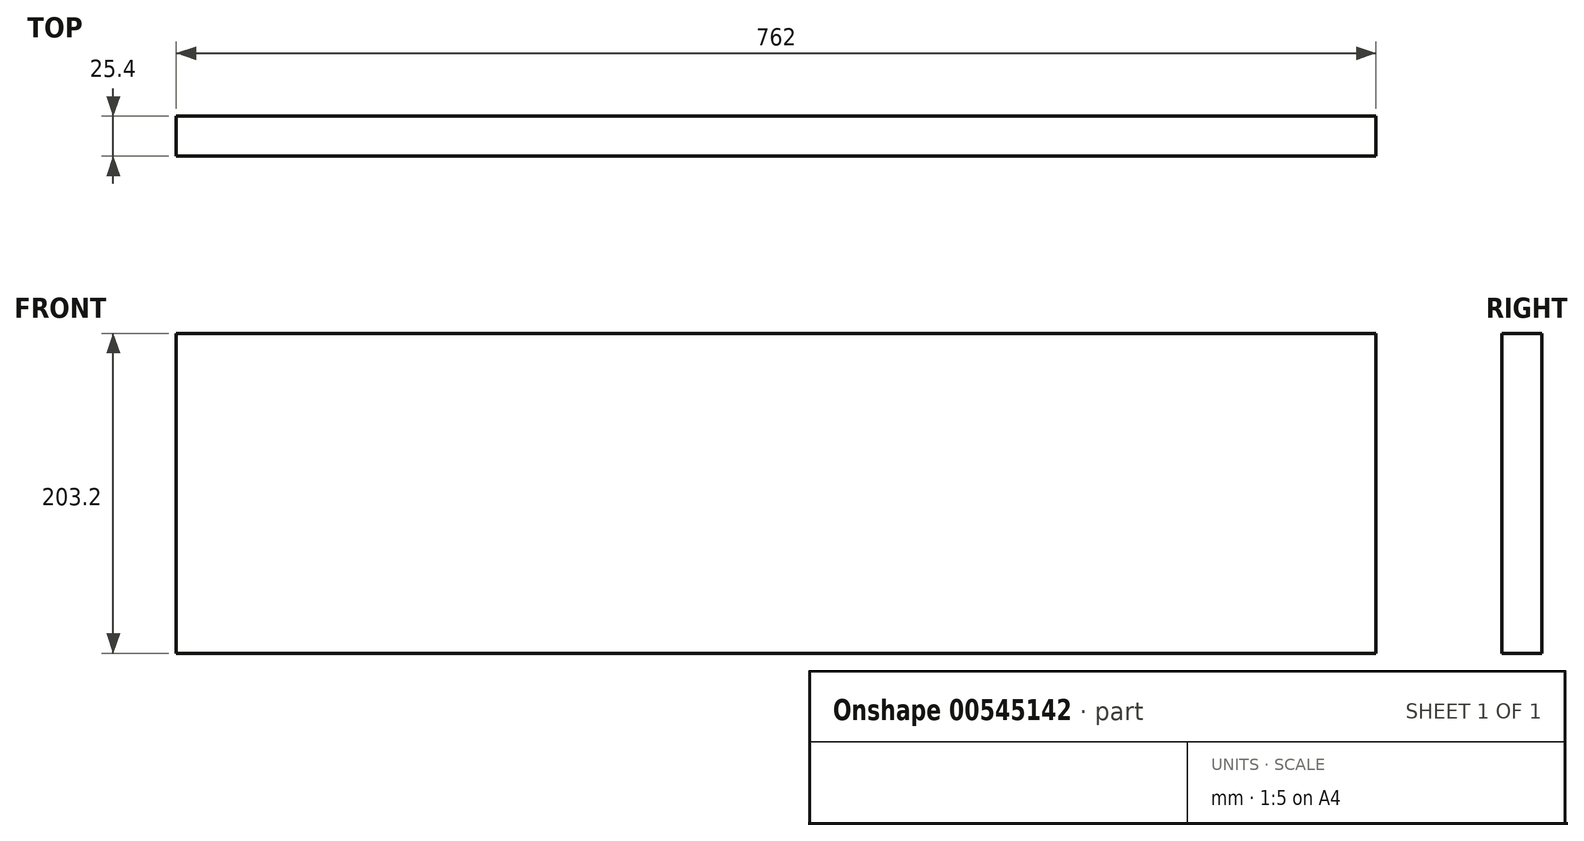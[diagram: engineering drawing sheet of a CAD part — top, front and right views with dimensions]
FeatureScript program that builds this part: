
annotation { "Feature Type Name" : "Feature", "Feature Type Description" : "" }
export const myFeature = defineFeature(function(context is Context, id is Id, definition is map)
    precondition{}
    {
        {
            var Q0;
            Q0=qCreatedBy(makeId("Front.planeOp"),FACE);
            var sketch = newSketch(context, id + "F0", { "sketchPlane" : qUnion([Q0])});
            skLineSegment(sketch, "E0.bottom", {"start": v(0, 0) * mm, "end": v(762, 0) * mm});
            skLineSegment(sketch, "E0.top", {"start": v(0, -203.2) * mm, "end": v(762, -203.2) * mm});
            skLineSegment(sketch, "E0.left", {"start": v(0, 0) * mm, "end": v(0, -203.2) * mm});
            skLineSegment(sketch, "E0.right", {"start": v(762, 0) * mm, "end": v(762, -203.2) * mm});
            skSolve(sketch);
        }
        {
            var Q0;
            Q0=makeQuery(id+"F0.imprint","IMPRINT",FACE,{"disambiguationData":[TD([[makeQuery(id+"F0.imprint","IMPRINT",EDGE,{"derivedFrom":sQuery(id+"F0.wireOp",EDGE,"E0.bottom")}),-1.0]])]});
            extrude(context, id + "F1", {"entities" : qUnion([Q0]), "depth" : 25.4 * mm, "offsetDistance" : 25.4 * mm});
        }
    });
